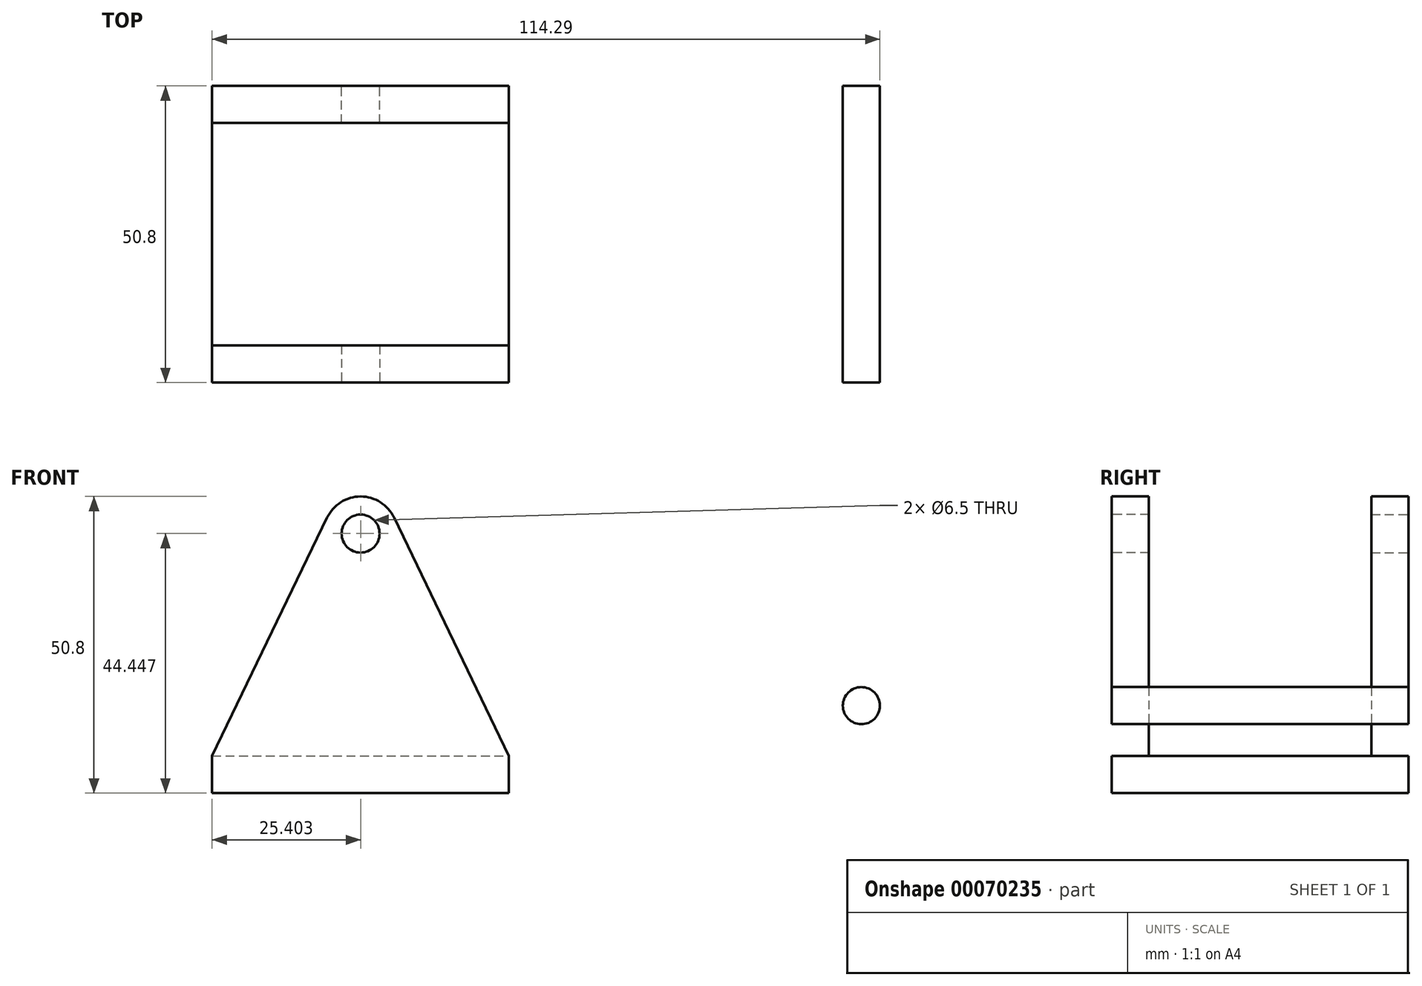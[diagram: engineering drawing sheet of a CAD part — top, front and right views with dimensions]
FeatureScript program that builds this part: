
annotation { "Feature Type Name" : "Feature", "Feature Type Description" : "" }
export const myFeature = defineFeature(function(context is Context, id is Id, definition is map)
    precondition{}
    {
        {
            var Q0;
            Q0=qCreatedBy(makeId("Front.planeOp"),FACE);
            var sketch = newSketch(context, id + "F0", { "sketchPlane" : qUnion([Q0])});
            skLineSegment(sketch, "E0.bottom", {"start": v(-72.23, 26.19) * mm, "end": v(-21.43, 26.19) * mm});
            skLineSegment(sketch, "E0.top", {"start": v(-72.23, 19.84) * mm, "end": v(-21.43, 19.84) * mm});
            skLineSegment(sketch, "E0.left", {"start": v(-72.23, 26.19) * mm, "end": v(-72.23, 19.84) * mm});
            skLineSegment(sketch, "E0.right", {"start": v(-21.43, 26.19) * mm, "end": v(-21.43, 19.84) * mm});
            skCircle(sketch, "E1", {"center": v(-46.83, 64.29) * mm, "radius": 6.35 * mm});
            skLineSegment(sketch, "E2", {"start": v(-52.55, 67.04) * mm, "end": v(-72.23, 26.19) * mm});
            skLineSegment(sketch, "E3", {"start": v(-41.1, 67.04) * mm, "end": v(-21.43, 26.19) * mm});
            skCircle(sketch, "E4", {"center": v(-46.83, 64.29) * mm, "radius": 3.25 * mm});
            skLineSegment(sketch, "E5", {"start": v(-46.83, 19.84) * mm, "end": v(-46.83, 58.41) * mm, "construction": true});
            skCircle(sketch, "E6", {"center": v(38.89, 34.82) * mm, "radius": 3.18 * mm});
            skSolve(sketch);
        }
        {
            var Q0;
            Q0=makeQuery(id+"F0.imprint","IMPRINT",FACE,{"disambiguationData":[TD([[makeQuery(id+"F0.imprint","IMPRINT",EDGE,{"derivedFrom":sQuery(id+"F0.wireOp",EDGE,"E6")}),1.0]])]});
            extrude(context, id + "F1", {"entities" : qUnion([Q0]), "depth" : 50.8 * mm});
        }
        {
            var Q0;
            Q0=makeQuery(id+"F0.imprint","IMPRINT",FACE,{"disambiguationData":[TD([[makeQuery(id+"F0.imprint","IMPRINT",EDGE,{"derivedFrom":sQuery(id+"F0.wireOp",EDGE,"E0.top")}),1.0]])]});
            extrude(context, id + "F2", {"entities" : qUnion([Q0]), "depth" : 50.8 * mm});
        }
        {
            var Q0;
            {var subQ0=sQuery(id+"F0.wireOp",EDGE,"E2");Q0=makeQuery(id+"F0.imprint","IMPRINT",FACE,{"disambiguationData":[TD([[makeQuery(id+"F0.imprint","IMPRINT",EDGE,{"derivedFrom":subQ0}),1.0]])]});}
            var Q1;
            Q1=makeQuery(id+"F0.imprint","IMPRINT",FACE,{"disambiguationData":[TD([[makeQuery(id+"F0.imprint","IMPRINT",EDGE,{"derivedFrom":sQuery(id+"F0.wireOp",EDGE,"E4")}),-1.0]])]});
            var Q2;
            {var subQ0=sQuery(id+"F0.wireOp",EDGE,"E3");Q2=makeQuery(id+"F0.imprint","IMPRINT",FACE,{"disambiguationData":[TD([[makeQuery(id+"F0.imprint","IMPRINT",EDGE,{"derivedFrom":subQ0}),-1.0]])]});}
            extrude(context, id + "F3", {"entities" : qUnion([Q0, Q1, Q2]), "operationType" : NewBodyOperationType.ADD, "depth" : 6.35 * mm});
        }
        {
            var Q0;
            Q0=makeQuery(id+"F2.opExtrude","CAP_FACE",FACE,{"disambiguationData":[OSD([sQuery(id+"F0.wireOp",EDGE,"E0.bottom"),sQuery(id+"F0.wireOp",EDGE,"E0.top"),sQuery(id+"F0.wireOp",EDGE,"E0.left"),sQuery(id+"F0.wireOp",EDGE,"E0.right")])],"isStart":false});
            var sketch = newSketch(context, id + "F4", { "sketchPlane" : qUnion([Q0])});
            skLineSegment(sketch, "E7.0", {"start": v(-52.55, 67.04) * mm, "end": v(-72.23, 26.19) * mm});
            skCircle(sketch, "E7.1", {"center": v(-46.83, 64.29) * mm, "radius": 3.25 * mm});
            skArc(sketch, "E7.2", {"start": v(-41.1, 67.04) * mm, "mid": v(-46.83, 70.64) * mm, "end": v(-52.55, 67.04) * mm});
            skLineSegment(sketch, "E7.3", {"start": v(-41.1, 67.04) * mm, "end": v(-21.43, 26.19) * mm});
            skLineSegment(sketch, "E7.4", {"start": v(-72.23, 26.19) * mm, "end": v(-21.43, 26.19) * mm});
            skSolve(sketch);
        }
        {
            var Q0;
            Q0=makeQuery(id+"F4.imprint","IMPRINT",FACE,{"disambiguationData":[TD([[makeQuery(id+"F4.imprint","IMPRINT",EDGE,{"derivedFrom":sQuery(id+"F4.wireOp",EDGE,"E7.0")}),1.0]])]});
            extrude(context, id + "F5", {"entities" : qUnion([Q0]), "operationType" : NewBodyOperationType.ADD, "oppositeDirection" : true, "depth" : 6.35 * mm});
        }
    });
